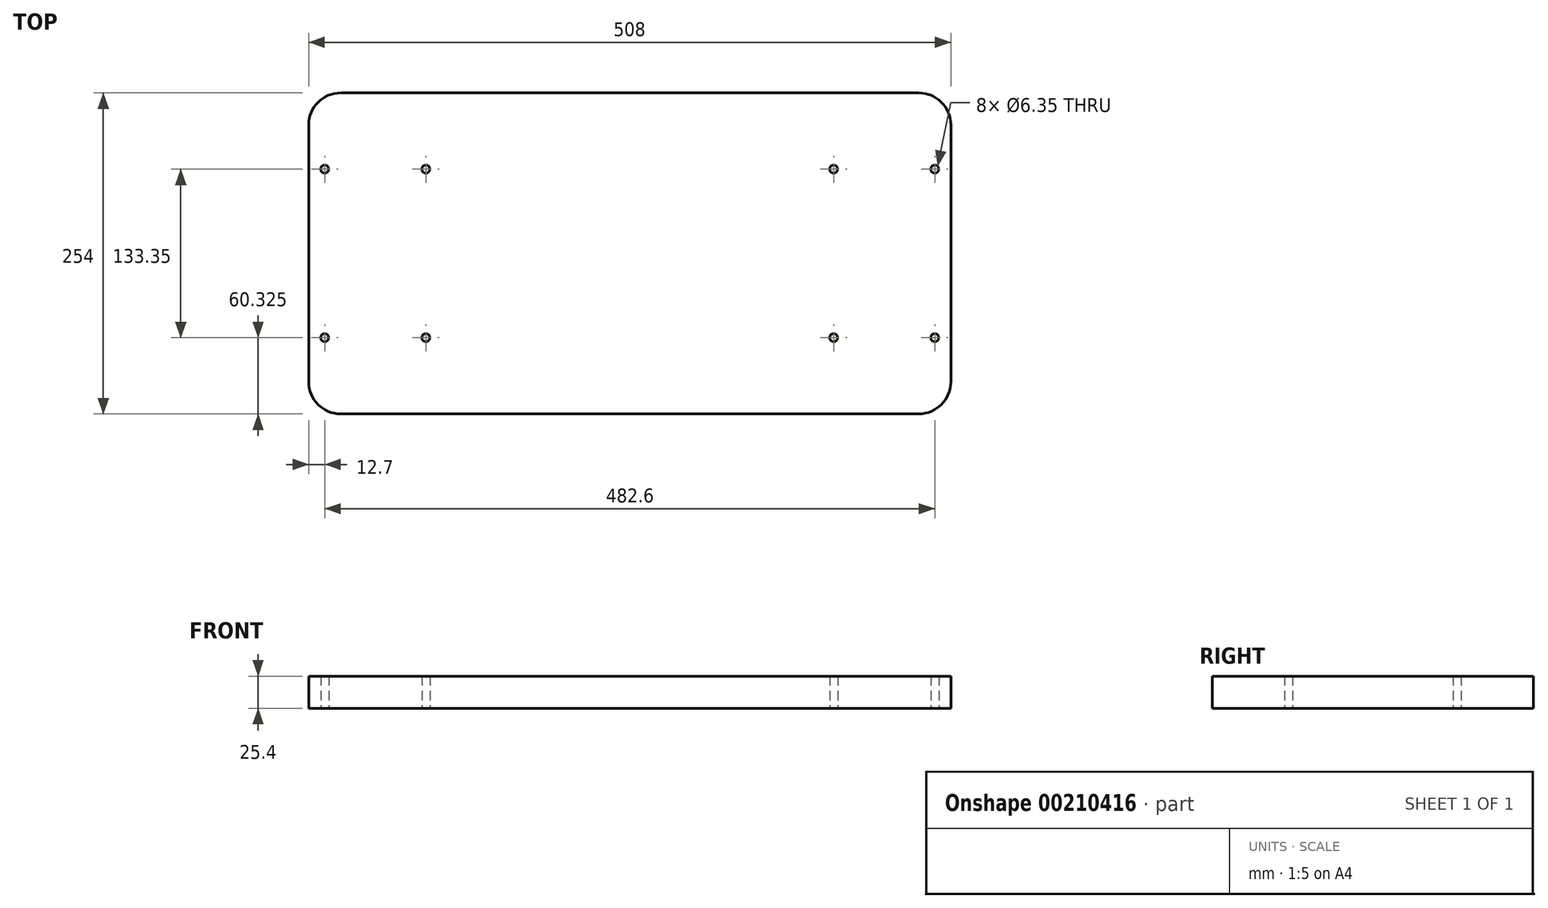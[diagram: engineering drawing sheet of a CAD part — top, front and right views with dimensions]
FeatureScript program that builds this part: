
annotation { "Feature Type Name" : "Feature", "Feature Type Description" : "" }
export const myFeature = defineFeature(function(context is Context, id is Id, definition is map)
    precondition{}
    {
        {
            var Q0;
            Q0=qCreatedBy(makeId("Top.planeOp"),FACE);
            var sketch = newSketch(context, id + "F0", { "sketchPlane" : qUnion([Q0])});
            skLineSegment(sketch, "E0.bottom", {"start": v(228.6, -127) * mm, "end": v(-228.6, -127) * mm});
            skLineSegment(sketch, "E0.top", {"start": v(228.6, 127) * mm, "end": v(-228.6, 127) * mm});
            skLineSegment(sketch, "E0.left", {"start": v(254, -101.6) * mm, "end": v(254, 101.6) * mm});
            skLineSegment(sketch, "E0.right", {"start": v(-254, -101.6) * mm, "end": v(-254, 101.6) * mm});
            skPoint(sketch, "E0.middle", {"position": v(0, 0) * mm});
            skPoint(sketch, "E1.visualSharp", {"position": v(-254, 127) * mm});
            skArc(sketch, "E1.filletArc", {"start": v(-228.6, 127) * mm, "mid": v(-246.56, 119.56) * mm, "end": v(-254, 101.6) * mm});
            skPoint(sketch, "E2.visualSharp", {"position": v(-254, -127) * mm});
            skArc(sketch, "E2.filletArc", {"start": v(-254, -101.6) * mm, "mid": v(-246.56, -119.56) * mm, "end": v(-228.6, -127) * mm});
            skPoint(sketch, "E3.visualSharp", {"position": v(254, 127) * mm});
            skArc(sketch, "E3.filletArc", {"start": v(254, 101.6) * mm, "mid": v(246.56, 119.56) * mm, "end": v(228.6, 127) * mm});
            skPoint(sketch, "E4.visualSharp", {"position": v(254, -127) * mm});
            skArc(sketch, "E4.filletArc", {"start": v(228.6, -127) * mm, "mid": v(246.56, -119.56) * mm, "end": v(254, -101.6) * mm});
            skSolve(sketch);
        }
        {
            var Q0;
            Q0=makeQuery(id+"F0.imprint","IMPRINT",FACE,{"disambiguationData":[TD([[makeQuery(id+"F0.imprint","IMPRINT",EDGE,{"derivedFrom":sQuery(id+"F0.wireOp",EDGE,"E0.bottom")}),-1.0]])]});
            extrude(context, id + "F1", {"entities" : qUnion([Q0]), "depth" : 25.4 * mm});
        }
        {
            var Q0;
            Q0=qCreatedBy(makeId("Top.planeOp"),FACE);
            var sketch = newSketch(context, id + "F2", { "sketchPlane" : qUnion([Q0])});
            skLineSegment(sketch, "E5", {"start": v(0, 0) * mm, "end": v(-254, 0) * mm, "construction": true});
            skLineSegment(sketch, "E6", {"start": v(0, 0) * mm, "end": v(254, 0) * mm, "construction": true});
            skLineSegment(sketch, "E7", {"start": v(0, 0) * mm, "end": v(0, 127) * mm, "construction": true});
            skLineSegment(sketch, "E8", {"start": v(0, 0) * mm, "end": v(0, -127) * mm, "construction": true});
            skPoint(sketch, "E9", {"position": v(-241.3, 66.67) * mm});
            skPoint(sketch, "E10", {"position": v(-161.29, 66.67) * mm});
            skPoint(sketch, "E11", {"position": v(-241.3, -66.68) * mm});
            skPoint(sketch, "E12", {"position": v(-161.29, -66.68) * mm});
            skPoint(sketch, "E13", {"position": v(241.3, -66.67) * mm});
            skPoint(sketch, "E14", {"position": v(161.29, 66.68) * mm});
            skPoint(sketch, "E15", {"position": v(241.3, 66.68) * mm});
            skPoint(sketch, "E16", {"position": v(161.29, -66.67) * mm});
            skSolve(sketch);
        }
        {
            var Q0;
            Q0=sQuery(id+"F2.wireOp",VERTEX,"E11");
            var Q1;
            Q1=sQuery(id+"F2.wireOp",VERTEX,"E12");
            var Q2;
            Q2=sQuery(id+"F2.wireOp",VERTEX,"E9");
            var Q3;
            Q3=sQuery(id+"F2.wireOp",VERTEX,"E10");
            var Q4;
            Q4=sQuery(id+"F2.wireOp",VERTEX,"E14");
            var Q5;
            Q5=sQuery(id+"F2.wireOp",VERTEX,"E15");
            var Q6;
            Q6=sQuery(id+"F2.wireOp",VERTEX,"E13");
            var Q7;
            Q7=sQuery(id+"F2.wireOp",VERTEX,"E16");
            var Q8;
            Q8=makeQuery(id+"F1.opExtrude","SWEPT_BODY",BODY,{"disambiguationData":[OSD([sQuery(id+"F0.wireOp",EDGE,"E0.bottom"),sQuery(id+"F0.wireOp",EDGE,"E0.top"),sQuery(id+"F0.wireOp",EDGE,"E0.left"),sQuery(id+"F0.wireOp",EDGE,"E0.right"),sQuery(id+"F0.wireOp",EDGE,"E1.filletArc"),sQuery(id+"F0.wireOp",EDGE,"E2.filletArc"),sQuery(id+"F0.wireOp",EDGE,"E3.filletArc"),sQuery(id+"F0.wireOp",EDGE,"E4.filletArc")])]});
            hole(context, id + "F3", {"style" : HoleStyle.SIMPLE, "endStyle" : HoleEndStyle.THROUGH, "oppositeDirection" : true, "holeDiameter" : 6.35 * mm, "locations" : qUnion([Q0, Q1, Q2, Q3, Q4, Q5, Q6, Q7]), "scope" : qUnion([Q8]), "isTappedThrough" : true});
        }
    });
